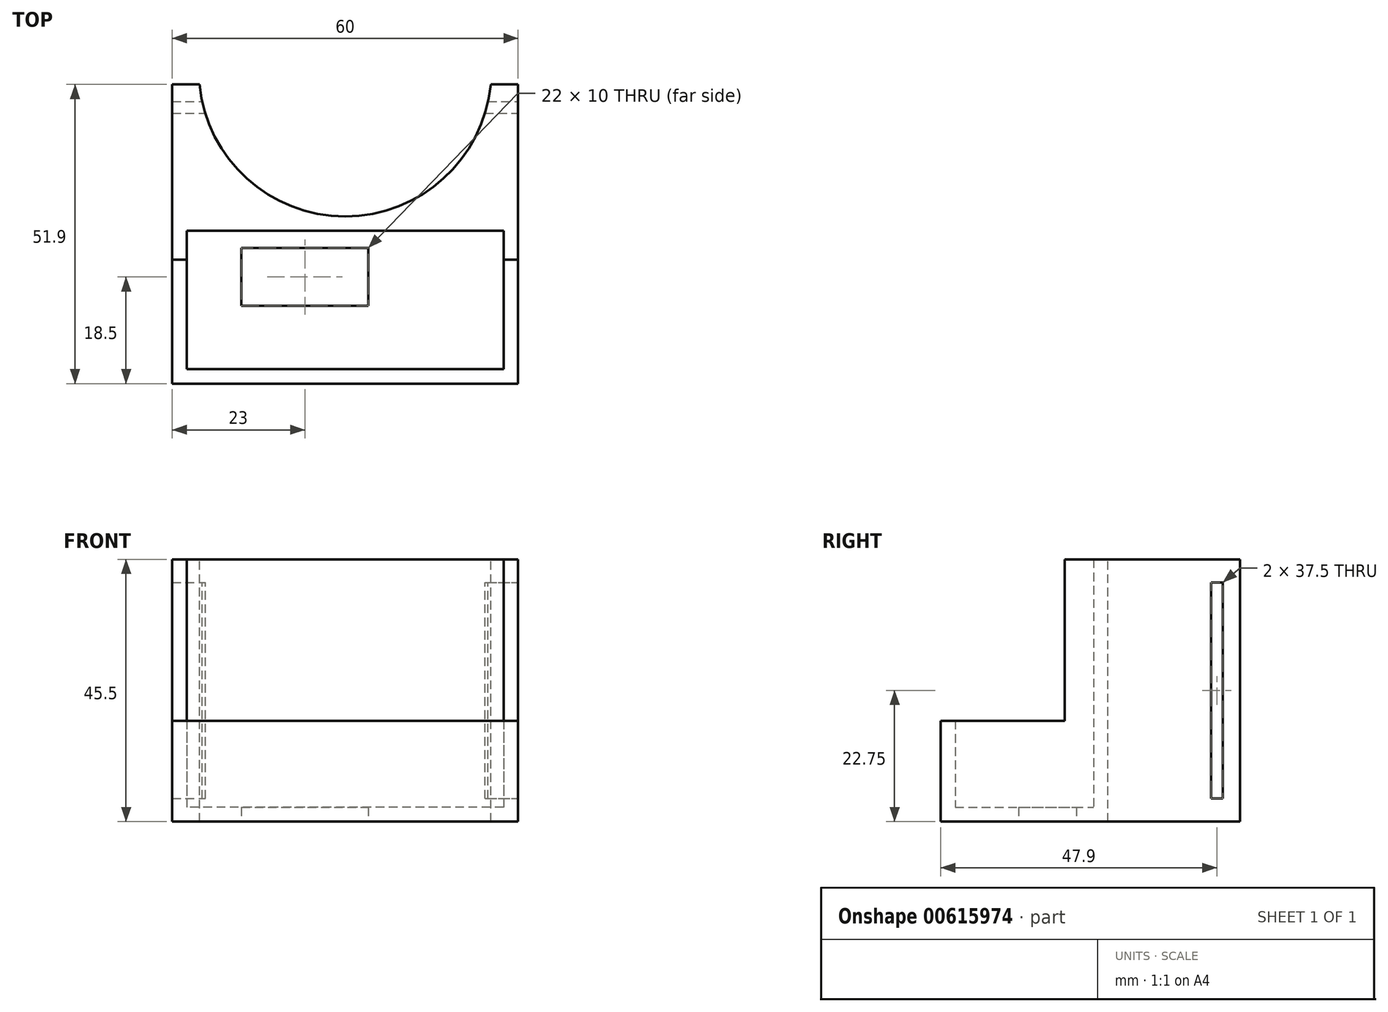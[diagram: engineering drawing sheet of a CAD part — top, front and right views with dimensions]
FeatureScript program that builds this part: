
annotation { "Feature Type Name" : "Feature", "Feature Type Description" : "" }
export const myFeature = defineFeature(function(context is Context, id is Id, definition is map)
    precondition{}
    {
        {
            var Q0;
            Q0=qCreatedBy(makeId("Front.planeOp"),FACE);
            var sketch = newSketch(context, id + "F0", { "sketchPlane" : qUnion([Q0])});
            skLineSegment(sketch, "E0.bottom", {"start": v(27.5, 27.5) * mm, "end": v(-27.5, 27.5) * mm});
            skLineSegment(sketch, "E0.top", {"start": v(27.5, -27.5) * mm, "end": v(-27.5, -27.5) * mm});
            skLineSegment(sketch, "E0.left", {"start": v(27.5, 27.5) * mm, "end": v(27.5, -27.5) * mm});
            skLineSegment(sketch, "E0.right", {"start": v(-27.5, 27.5) * mm, "end": v(-27.5, -27.5) * mm});
            skPoint(sketch, "E0.middle", {"position": v(0, 0) * mm});
            skSolve(sketch);
        }
        {
            var Q0;
            Q0=makeQuery(id+"F0.imprint","IMPRINT",FACE,{"disambiguationData":[TD([[makeQuery(id+"F0.imprint","IMPRINT",EDGE,{"derivedFrom":sQuery(id+"F0.wireOp",EDGE,"E0.bottom")}),1.0]])]});
            extrude(context, id + "F1", {"entities" : qUnion([Q0]), "depth" : 24 * mm, "offsetDistance" : 25 * mm});
        }
        {
            var Q0;
            Q0=makeQuery(id+"F1.opExtrude","SWEPT_FACE",FACE,{"disambiguationData":[OSD([sQuery(id+"F0.wireOp",EDGE,"E0.top")])]});
            var sketch = newSketch(context, id + "F2", { "sketchPlane" : qUnion([Q0])});
            skLineSegment(sketch, "E1.bottom", {"start": v(30, 26.5) * mm, "end": v(-30, 26.5) * mm, "construction": true});
            skLineSegment(sketch, "E1.top", {"start": v(30, -2.5) * mm, "end": v(-30, -2.5) * mm, "construction": true});
            skLineSegment(sketch, "E1.left", {"start": v(30, 26.5) * mm, "end": v(30, -2.5) * mm, "construction": true});
            skLineSegment(sketch, "E1.right", {"start": v(-30, 26.5) * mm, "end": v(-30, -2.5) * mm, "construction": true});
            skLineSegment(sketch, "E2.bottom", {"start": v(-30, 26.5) * mm, "end": v(30, 26.5) * mm});
            skLineSegment(sketch, "E2.top", {"start": v(-30, -2.5) * mm, "end": v(30, -2.5) * mm});
            skLineSegment(sketch, "E2.left", {"start": v(-30, 26.5) * mm, "end": v(-30, -2.5) * mm});
            skLineSegment(sketch, "E2.right", {"start": v(30, 26.5) * mm, "end": v(30, -2.5) * mm});
            skSolve(sketch);
        }
        {
            var Q0;
            Q0=qSketchRegion(id+"F2",true);
            extrude(context, id + "F3", {"entities" : qUnion([Q0]), "operationType" : NewBodyOperationType.ADD, "depth" : 2.5 * mm, "offsetDistance" : 25 * mm});
        }
        {
            var Q0;
            Q0=qSketchRegion(id+"F2",true);
            extrude(context, id + "F4", {"entities" : qUnion([Q0]), "operationType" : NewBodyOperationType.ADD, "oppositeDirection" : true, "depth" : 15 * mm, "offsetDistance" : 25 * mm});
        }
        {
            var Q0;
            Q0=makeQuery(id+"F3.opExtrude","CAP_FACE",FACE,{"disambiguationData":[OSD([sQuery(id+"F2.wireOp",EDGE,"E2.bottom"),sQuery(id+"F2.wireOp",EDGE,"E2.top"),sQuery(id+"F2.wireOp",EDGE,"E2.left"),sQuery(id+"F2.wireOp",EDGE,"E2.right")])],"isStart":false});
            var sketch = newSketch(context, id + "F5", { "sketchPlane" : qUnion([Q0])});
            skLineSegment(sketch, "E3.bottom", {"start": v(-18, 13) * mm, "end": v(4, 13) * mm});
            skLineSegment(sketch, "E3.top", {"start": v(-18, 3) * mm, "end": v(4, 3) * mm});
            skLineSegment(sketch, "E3.left", {"start": v(-18, 13) * mm, "end": v(-18, 3) * mm});
            skLineSegment(sketch, "E3.right", {"start": v(4, 13) * mm, "end": v(4, 3) * mm});
            skSolve(sketch);
        }
        {
            var Q0;
            Q0=qSketchRegion(id+"F5",true);
            extrude(context, id + "F6", {"entities" : qUnion([Q0]), "operationType" : NewBodyOperationType.REMOVE, "oppositeDirection" : true, "depth" : 2.5 * mm, "offsetDistance" : 25 * mm});
        }
        {
            var Q0;
            Q0=makeQuery(id+"F4.opExtrude","CAP_FACE",FACE,{"disambiguationData":[OSD([sQuery(id+"F2.wireOp",EDGE,"E2.bottom"),sQuery(id+"F2.wireOp",EDGE,"E2.top"),sQuery(id+"F2.wireOp",EDGE,"E2.left"),sQuery(id+"F2.wireOp",EDGE,"E2.right")])],"isStart":false});
            var sketch = newSketch(context, id + "F7", { "sketchPlane" : qUnion([Q0])});
            skLineSegment(sketch, "E4.bottom", {"start": v(-30, 2.5) * mm, "end": v(30, 2.5) * mm});
            skLineSegment(sketch, "E4.top", {"start": v(-30, 0) * mm, "end": v(30, 0) * mm});
            skLineSegment(sketch, "E4.left", {"start": v(-30, 2.5) * mm, "end": v(-30, 0) * mm});
            skLineSegment(sketch, "E4.right", {"start": v(30, 2.5) * mm, "end": v(30, 0) * mm});
            skLineSegment(sketch, "E5.bottom", {"start": v(30, 0) * mm, "end": v(27.5, 0) * mm});
            skLineSegment(sketch, "E5.top", {"start": v(30, -5) * mm, "end": v(27.5, -5) * mm});
            skLineSegment(sketch, "E5.left", {"start": v(30, 0) * mm, "end": v(30, -5) * mm});
            skLineSegment(sketch, "E5.right", {"start": v(27.5, 0) * mm, "end": v(27.5, -5) * mm});
            skLineSegment(sketch, "E6.bottom", {"start": v(-30, 0) * mm, "end": v(-27.5, 0) * mm});
            skLineSegment(sketch, "E6.top", {"start": v(-30, -5) * mm, "end": v(-27.5, -5) * mm});
            skLineSegment(sketch, "E6.left", {"start": v(-30, 0) * mm, "end": v(-30, -5) * mm});
            skLineSegment(sketch, "E6.right", {"start": v(-27.5, 0) * mm, "end": v(-27.5, -5) * mm});
            skSolve(sketch);
        }
        {
            var Q0;
            Q0=qSketchRegion(id+"F7",true);
            extrude(context, id + "F8", {"entities" : qUnion([Q0]), "operationType" : NewBodyOperationType.ADD, "depth" : 28 * mm, "offsetDistance" : 25 * mm});
        }
        {
            var Q0;
            {var subQ0=sQuery(id+"F2.wireOp",EDGE,"E2.top");Q0=makeQuery(id+"F8.boolean.opBoolean","MERGE",FACE,{"derivedFrom":[makeQuery(id+"F4.boolean.opBoolean","MERGE",FACE,{"derivedFrom":[makeQuery(id+"F3.opExtrude","SWEPT_FACE",FACE,{"disambiguationData":[OSD([subQ0])]}),makeQuery(id+"F4.opExtrude","SWEPT_FACE",FACE,{"disambiguationData":[OSD([subQ0])]})]}),makeQuery(id+"F8.opExtrude","SWEPT_FACE",FACE,{"disambiguationData":[OSD([sQuery(id+"F7.wireOp",EDGE,"E4.bottom")])]})]});}
            extrude(context, id + "F9", {"entities" : qUnion([Q0]), "operationType" : NewBodyOperationType.ADD, "depth" : 25.4 * mm, "offsetDistance" : 25 * mm});
        }
        {
            var Q0;
            {var subQ0=sQuery(id+"F7.wireOp",EDGE,"E4.bottom");Q0=makeQuery(id+"F9.boolean.opBoolean","MERGE",FACE,{"derivedFrom":[makeQuery(id+"F8.opExtrude","CAP_FACE",FACE,{"disambiguationData":[OSD([subQ0,sQuery(id+"F7.wireOp",EDGE,"E4.top"),sQuery(id+"F7.wireOp",EDGE,"E4.left"),sQuery(id+"F7.wireOp",EDGE,"E4.right"),sQuery(id+"F7.wireOp",EDGE,"E5.top"),sQuery(id+"F7.wireOp",EDGE,"E5.left"),sQuery(id+"F7.wireOp",EDGE,"E5.right"),sQuery(id+"F7.wireOp",EDGE,"E6.top"),sQuery(id+"F7.wireOp",EDGE,"E6.left"),sQuery(id+"F7.wireOp",EDGE,"E6.right")])],"isStart":false}),makeQuery(id+"F9.opExtrude","SWEPT_FACE",FACE,{"disambiguationData":[OSD([subQ0])]})]});}
            var sketch = newSketch(context, id + "F10", { "sketchPlane" : qUnion([Q0])});
            skCircle(sketch, "E7", {"center": v(0, 27.9) * mm, "radius": 25.4 * mm});
            skLineSegment(sketch, "E8.bottom", {"start": v(30, 27.9) * mm, "end": v(-30, 27.9) * mm});
            skLineSegment(sketch, "E8.top", {"start": v(30, 25.4) * mm, "end": v(-30, 25.4) * mm});
            skLineSegment(sketch, "E8.left", {"start": v(30, 27.9) * mm, "end": v(30, 25.4) * mm});
            skLineSegment(sketch, "E8.right", {"start": v(-30, 27.9) * mm, "end": v(-30, 25.4) * mm});
            skSolve(sketch);
        }
        {
            var Q0;
            Q0=qSketchRegion(id+"F10",true);
            extrude(context, id + "F11", {"entities" : qUnion([Q0]), "operationType" : NewBodyOperationType.REMOVE, "oppositeDirection" : true, "depth" : 46 * mm, "offsetDistance" : 25 * mm});
        }
        {
            var Q0;
            {var subQ0=sQuery(id+"F7.wireOp",EDGE,"E4.right");var subQ1=sQuery(id+"F2.wireOp",EDGE,"E2.right");Q0=makeQuery(id+"F9.boolean.opBoolean","MERGE",FACE,{"derivedFrom":[makeQuery(id+"F8.boolean.opBoolean","MERGE",FACE,{"derivedFrom":[makeQuery(id+"F4.boolean.opBoolean","MERGE",FACE,{"derivedFrom":[makeQuery(id+"F3.opExtrude","SWEPT_FACE",FACE,{"disambiguationData":[OSD([subQ1])]}),makeQuery(id+"F4.opExtrude","SWEPT_FACE",FACE,{"disambiguationData":[OSD([subQ1])]})]}),makeQuery(id+"F8.opExtrude","SWEPT_FACE",FACE,{"disambiguationData":[OSD([subQ0,sQuery(id+"F7.wireOp",EDGE,"E5.left")])]})]}),makeQuery(id+"F9.opExtrude","SWEPT_FACE",FACE,{"disambiguationData":[OSD([sQuery(id+"F2.wireOp",EDGE,"E2.top"),subQ1,sQuery(id+"F7.wireOp",EDGE,"E4.bottom"),subQ0])]})]});}
            var sketch = newSketch(context, id + "F12", { "sketchPlane" : qUnion([Q0])});
            skLineSegment(sketch, "E9.bottom", {"start": v(22.4, 11.5) * mm, "end": v(20.4, 11.5) * mm});
            skLineSegment(sketch, "E9.top", {"start": v(22.4, -26) * mm, "end": v(20.4, -26) * mm});
            skLineSegment(sketch, "E9.left", {"start": v(22.4, 11.5) * mm, "end": v(22.4, -26) * mm});
            skLineSegment(sketch, "E9.right", {"start": v(20.4, 11.5) * mm, "end": v(20.4, -26) * mm});
            skSolve(sketch);
        }
        {
            var Q0;
            Q0=qSketchRegion(id+"F12",true);
            extrude(context, id + "F13", {"entities" : qUnion([Q0]), "operationType" : NewBodyOperationType.REMOVE, "oppositeDirection" : true, "depth" : 60 * mm, "offsetDistance" : 25 * mm});
        }
        {
            var Q0;
            Q0=qSketchRegion(id+"F0",true);
            extrude(context, id + "F14", {"entities" : qUnion([Q0]), "operationType" : NewBodyOperationType.REMOVE, "depth" : 24 * mm, "offsetDistance" : 25 * mm});
        }
    });
